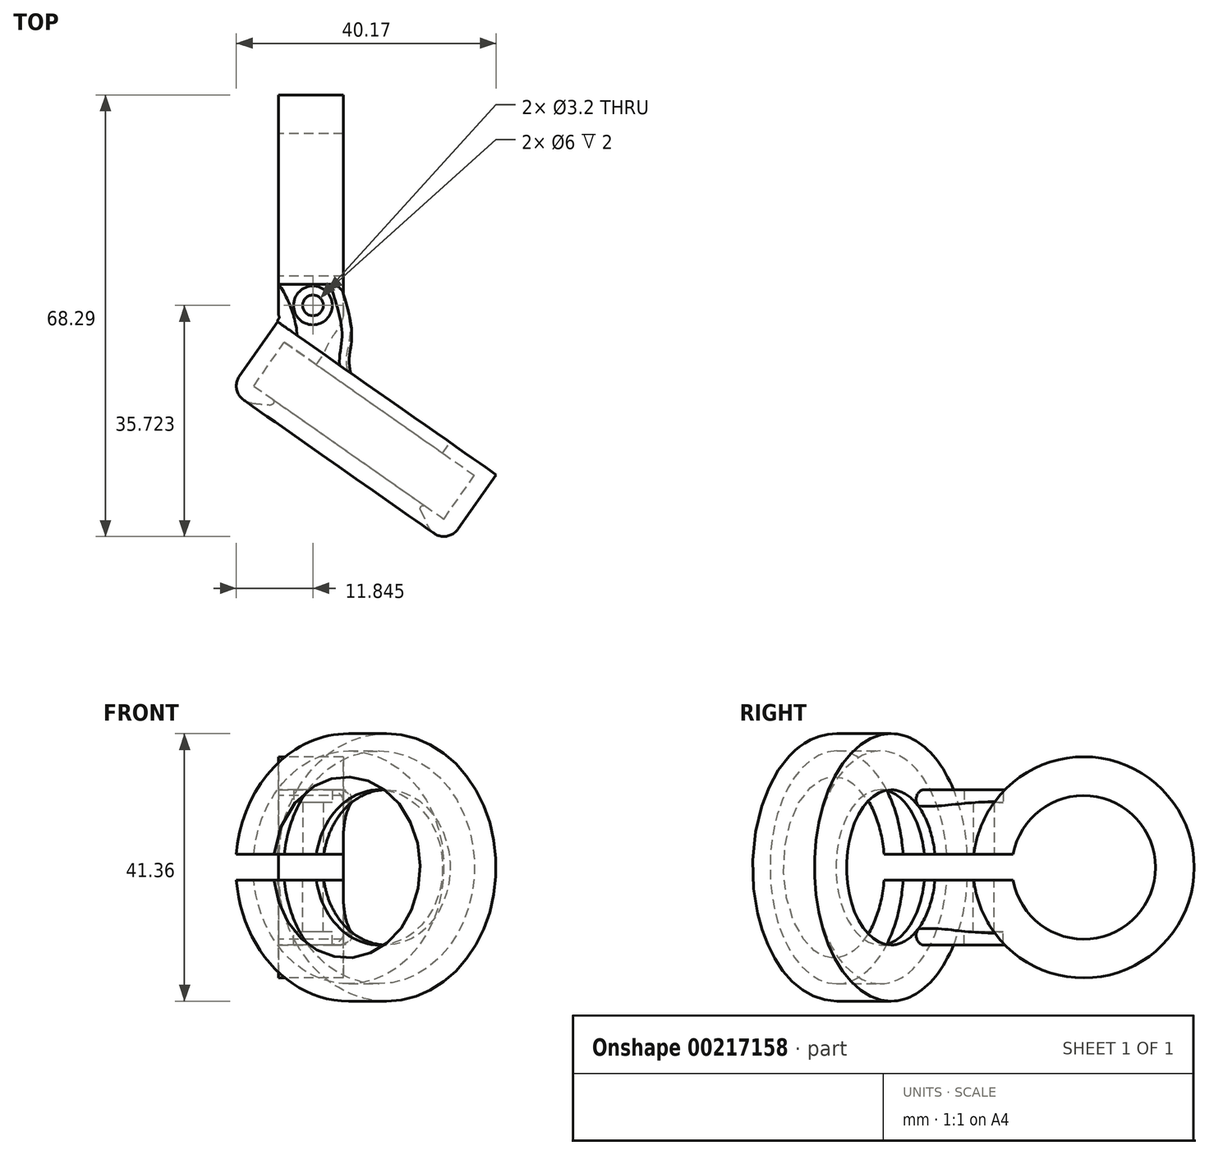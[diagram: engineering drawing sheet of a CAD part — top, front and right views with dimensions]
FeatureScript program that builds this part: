
annotation { "Feature Type Name" : "Feature", "Feature Type Description" : "" }
export const myFeature = defineFeature(function(context is Context, id is Id, definition is map)
    precondition{}
    {
        {
            var Q0;
            Q0=qCreatedBy(makeId("Top.planeOp"),FACE);
            var sketch = newSketch(context, id + "F0", { "sketchPlane" : qUnion([Q0])});
            skLineSegment(sketch, "E0.bottom", {"start": v(-17.11, 22.2) * mm, "end": v(17.11, 22.2) * mm});
            skLineSegment(sketch, "E0.top", {"start": v(-17.11, 0) * mm, "end": v(17.11, 0) * mm});
            skLineSegment(sketch, "E0.left", {"start": v(-17.11, 22.2) * mm, "end": v(-17.11, 0) * mm});
            skLineSegment(sketch, "E0.right", {"start": v(17.11, 22.2) * mm, "end": v(17.11, 0) * mm});
            skLineSegment(sketch, "E1", {"start": v(-12.38, -10) * mm, "end": v(-17.11, -16.76) * mm});
            skLineSegment(sketch, "E2", {"start": v(-17.11, -16.76) * mm, "end": v(12.38, -37.4) * mm});
            skLineSegment(sketch, "E3", {"start": v(12.38, -37.4) * mm, "end": v(17.11, -30.65) * mm});
            skLineSegment(sketch, "E4", {"start": v(17.11, -30.65) * mm, "end": v(-12.38, -10) * mm});
            skLineSegment(sketch, "E5", {"start": v(-2.37, -27.08) * mm, "end": v(2.37, -20.32) * mm});
            skLineSegment(sketch, "E6", {"start": v(-17.11, 11.1) * mm, "end": v(17.11, 11.1) * mm});
            skSolve(sketch);
        }
        {
            var Q0;
            Q0=qCreatedBy(makeId("Top.planeOp"),FACE);
            var sketch = newSketch(context, id + "F1", { "sketchPlane" : qUnion([Q0])});
            skLineSegment(sketch, "E7", {"start": v(-14.57, -19.67) * mm, "end": v(-17.34, -19.43) * mm});
            skArc(sketch, "E8", {"start": v(-14.57, -19.67) * mm, "mid": v(-14.06, -19.35) * mm, "end": v(-14.24, -18.77) * mm});
            skLineSegment(sketch, "E9", {"start": v(-14.24, -18.77) * mm, "end": v(-17.11, -16.76) * mm});
            skLineSegment(sketch, "E10", {"start": v(-17.11, -16.76) * mm, "end": v(-12.38, -10) * mm});
            skArc(sketch, "E11", {"start": v(-19.3, -15.22) * mm, "mid": v(-19.54, -17.9) * mm, "end": v(-17.34, -19.43) * mm});
            skLineSegment(sketch, "E12", {"start": v(-19.3, -15.22) * mm, "end": v(-13.43, -6.82) * mm});
            skLineSegment(sketch, "E13", {"start": v(-12.38, -10) * mm, "end": v(-7.46, -13.44) * mm});
            skLineSegment(sketch, "E14", {"start": v(-7.46, -13.44) * mm, "end": v(-6.32, -11.8) * mm});
            skLineSegment(sketch, "E15", {"start": v(-6.32, -11.8) * mm, "end": v(-13.43, -6.82) * mm});
            skSolve(sketch);
        }
        {
            var Q0;
            Q0 = qSketchRegion(id + "F1", true);
            var Q1;
            Q1=sQuery(id+"F0.wireOp",EDGE,"E5");
            revolve(context, id + "F2", {"entities" : qUnion([Q0]), "axis" : qUnion([Q1]), "revolveType" : RevolveType.ONE_DIRECTION, "oppositeDirection" : true, "angle" : 180 * degree});
        }
        {
            var Q0;
            Q0=qCreatedBy(makeId("Top.planeOp"),FACE);
            var sketch = newSketch(context, id + "F3", { "sketchPlane" : qUnion([Q0])});
            skLineSegment(sketch, "E16", {"start": v(-13.17, 0) * mm, "end": v(-13.17, -6) * mm});
            skLineSegment(sketch, "E17", {"start": v(-13.17, -6) * mm, "end": v(-3.17, -6) * mm});
            skLineSegment(sketch, "E18", {"start": v(-3.17, -6) * mm, "end": v(-3.17, 0) * mm});
            skLineSegment(sketch, "E19", {"start": v(-3.17, 0) * mm, "end": v(-13.17, 0) * mm});
            skArc(sketch, "E20", {"start": v(-13.43, -6.82) * mm, "mid": v(-13.24, -6.43) * mm, "end": v(-13.17, -6) * mm, "construction": true});
            skSolve(sketch);
        }
        {
            var Q0;
            Q0=makeQuery(id+"F3.imprint","IMPRINT",FACE,{"disambiguationData":[TD([[makeQuery(id+"F3.imprint","IMPRINT",EDGE,{"derivedFrom":sQuery(id+"F3.wireOp",EDGE,"E16")}),1.0]])]});
            var Q1;
            Q1=sQuery(id+"F0.wireOp",EDGE,"E6");
            revolve(context, id + "F4", {"entities" : qUnion([Q0]), "axis" : qUnion([Q1]), "revolveType" : RevolveType.ONE_DIRECTION, "angle" : 180 * degree});
        }
        {
            var Q0;
            Q0=qCreatedBy(makeId("Top.planeOp"),FACE);
            cPlane(context, id + "F5", {"entities" : qUnion([Q0]), "cplaneType" : CPlaneType.OFFSET, "offset" : 12 * mm, "oppositeDirection" : true, "width" : 150 * mm, "height" : 150 * mm});
        }
        {
            var Q0;
            Q0=qCreatedBy(id+"F5.planeOp",FACE);
            var sketch = newSketch(context, id + "F6", { "sketchPlane" : qUnion([Q0])});
            skLineSegment(sketch, "E21", {"start": v(-13.17, -1.08) * mm, "end": v(-3.17, -1.08) * mm});
            skLineSegment(sketch, "E22", {"start": v(-3.17, 23.28) * mm, "end": v(-13.17, 23.28) * mm});
            skLineSegment(sketch, "E23", {"start": v(3.51, -18.69) * mm, "end": v(-10.29, -9.02) * mm});
            skLineSegment(sketch, "E24", {"start": v(3.51, -18.69) * mm, "end": v(-3.17, -1.08) * mm});
            skArc(sketch, "E25", {"start": v(-10.29, -9.02) * mm, "mid": v(-11.21, -4.87) * mm, "end": v(-13.17, -1.08) * mm});
            skSolve(sketch);
        }
        {
            var Q0;
            Q0=makeQuery(id+"F4.opRevolve","CAP_FACE",FACE,{"disambiguationData":[OSD([sQuery(id+"F3.wireOp",EDGE,"E16"),sQuery(id+"F3.wireOp",EDGE,"E17"),sQuery(id+"F3.wireOp",EDGE,"E18"),sQuery(id+"F3.wireOp",EDGE,"E19")])],"isStart":true});
            var sketch = newSketch(context, id + "F7", { "sketchPlane" : qUnion([Q0])});
            skLineSegment(sketch, "E26", {"start": v(-13.17, -6) * mm, "end": v(-3.17, -6) * mm});
            skLineSegment(sketch, "E27", {"start": v(-3.17, -6) * mm, "end": v(-6.32, -11.8) * mm});
            skLineSegment(sketch, "E28", {"start": v(-6.32, -11.8) * mm, "end": v(-13.43, -6.82) * mm});
            skArc(sketch, "E29.0", {"start": v(-13.43, -6.82) * mm, "mid": v(-13.24, -6.43) * mm, "end": v(-13.17, -6) * mm});
            skSolve(sketch);
        }
        {
            var Q0;
            Q0=makeQuery(id+"F4.opRevolve","SWEPT_FACE",FACE,{"disambiguationData":[OSD([sQuery(id+"F3.wireOp",EDGE,"E16")])]});
            var sketch = newSketch(context, id + "F8", { "sketchPlane" : qUnion([Q0])});
            skArc(sketch, "E30.0", {"start": v(1.08, -12) * mm, "mid": v(4.72, -6.48) * mm, "end": v(6, 0) * mm});
            skPoint(sketch, "E31", {"position": v(1.08, -12) * mm});
            skPoint(sketch, "E32.orphan", {"position": v(-28.2, 0) * mm});
            skSolve(sketch);
        }
        {
            var Q0;
            Q0=makeQuery(id+"F2.opRevolve","SWEPT_FACE",FACE,{"disambiguationData":[OSD([sQuery(id+"F1.wireOp",EDGE,"E15")])]});
            var sketch = newSketch(context, id + "F9", { "sketchPlane" : qUnion([Q0])});
            skArc(sketch, "E33.0", {"start": v(-13.6, -12) * mm, "mid": v(-5.11, -8.49) * mm, "end": v(-1.6, 0) * mm});
            skArc(sketch, "E33.1", {"start": v(3.25, -12) * mm, "mid": v(6.1, -6.3) * mm, "end": v(7.09, 0) * mm});
            skPoint(sketch, "E34", {"position": v(-13.6, -12) * mm});
            skPoint(sketch, "E35", {"position": v(3.25, -12) * mm});
            skSolve(sketch);
        }
        {
            var Q0;
            Q0=makeQuery(id+"F4.opRevolve","SWEPT_FACE",FACE,{"disambiguationData":[OSD([sQuery(id+"F3.wireOp",EDGE,"E18")])]});
            var sketch = newSketch(context, id + "F10", { "sketchPlane" : qUnion([Q0])});
            skArc(sketch, "E36.0", {"start": v(-1.08, -12) * mm, "mid": v(-4.72, -6.48) * mm, "end": v(-6, 0) * mm});
            skPoint(sketch, "E37", {"position": v(-1.08, -12) * mm});
            skSolve(sketch);
        }
        {
            var Q2;
            Q2=makeQuery(id+"F7.imprint","IMPRINT",FACE,{"disambiguationData":[TD([[makeQuery(id+"F7.imprint","IMPRINT",EDGE,{"derivedFrom":sQuery(id+"F7.wireOp",EDGE,"E26")}),-1.0]])]});
            var Q3;
            Q3=makeQuery(id+"F6.imprint","IMPRINT",FACE,{"disambiguationData":[TD([[makeQuery(id+"F6.imprint","IMPRINT",EDGE,{"derivedFrom":sQuery(id+"F6.wireOp",EDGE,"E21")}),-1.0]])]});
            var Q4;
            Q4=sQuery(id+"F9.wireOp",EDGE,"E33.0");
            var Q5;
            Q5=sQuery(id+"F10.wireOp",EDGE,"E36.0");
            var Q6;
            Q6=sQuery(id+"F8.wireOp",EDGE,"E30.0");
            var Q7;
            Q7=sQuery(id+"F9.wireOp",EDGE,"E33.1");
            loft(context, id + "F11", {"operationType" : NewBodyOperationType.ADD, "addGuides" : true, "sheetProfilesArray" : [{ "sheetProfileEntities" : qUnion([Q2]) }, { "sheetProfileEntities" : qUnion([Q3]) }], "guidesArray" : [{ "guideEntities" : qUnion([Q4]), "guideDerivativeType" : LoftGuideDerivativeType.DEFAULT, "guideDerivativeMagnitude" : 1 }, { "guideEntities" : qUnion([Q5]), "guideDerivativeType" : LoftGuideDerivativeType.DEFAULT, "guideDerivativeMagnitude" : 1 }, { "guideEntities" : qUnion([Q6]), "guideDerivativeType" : LoftGuideDerivativeType.DEFAULT, "guideDerivativeMagnitude" : 1 }, { "guideEntities" : qUnion([Q7]), "guideDerivativeType" : LoftGuideDerivativeType.DEFAULT, "guideDerivativeMagnitude" : 1 }]});
        }
        {
            var Q0;
            Q0=qCreatedBy(makeId("Top.planeOp"),FACE);
            var sketch = newSketch(context, id + "F12", { "sketchPlane" : qUnion([Q0])});
            skLineSegment(sketch, "E38.bottom", {"start": v(-24.47, 6.44) * mm, "end": v(1.46, 6.44) * mm});
            skLineSegment(sketch, "E38.top", {"start": v(-24.47, -24.77) * mm, "end": v(1.46, -24.77) * mm});
            skLineSegment(sketch, "E38.left", {"start": v(-24.47, 6.44) * mm, "end": v(-24.47, -24.77) * mm});
            skLineSegment(sketch, "E38.right", {"start": v(1.46, 6.44) * mm, "end": v(1.46, -24.77) * mm});
            skSolve(sketch);
        }
        {
            var Q0;
            Q0=makeQuery(id+"F12.imprint","IMPRINT",FACE,{"disambiguationData":[TD([[makeQuery(id+"F12.imprint","IMPRINT",EDGE,{"derivedFrom":sQuery(id+"F12.wireOp",EDGE,"E38.bottom")}),-1.0]])]});
            extrude(context, id + "F13", {"entities" : qUnion([Q0]), "operationType" : NewBodyOperationType.REMOVE, "oppositeDirection" : true, "depth" : 2 * mm});
        }
        {
            var Q0;
            Q0=qCreatedBy(makeId("Top.planeOp"),FACE);
            var sketch = newSketch(context, id + "F14", { "sketchPlane" : qUnion([Q0])});
            skCircle(sketch, "E39", {"center": v(-7.86, -4.37) * mm, "radius": 1.6 * mm});
            skSolve(sketch);
        }
        {
            var Q0;
            Q0 = qSketchRegion(id + "F14", true);
            extrude(context, id + "F15", {"entities" : qUnion([Q0]), "operationType" : NewBodyOperationType.REMOVE, "oppositeDirection" : true, "depth" : 10 * mm});
        }
        {
            var Q0;
            Q0=makeQuery(id+"F15.boolean.opBoolean","COPY",FACE,{"derivedFrom":makeQuery(id+"F15.opExtrude","CAP_FACE",FACE,{"disambiguationData":[OSD([sQuery(id+"F14.wireOp",EDGE,"E39")])],"isStart":false})});
            var sketch = newSketch(context, id + "F16", { "sketchPlane" : qUnion([Q0])});
            skCircle(sketch, "E40", {"center": v(-7.86, -4.37) * mm, "radius": 3 * mm});
            skSolve(sketch);
        }
        {
            var Q0;
            Q0 = qSketchRegion(id + "F16", true);
            extrude(context, id + "F17", {"entities" : qUnion([Q0]), "operationType" : NewBodyOperationType.REMOVE, "oppositeDirection" : true, "depth" : 25 * mm});
        }
        {
            var Q0;
            Q0=makeQuery(id+"F11.opLoft","MID_CAP_EDGE",EDGE,{"disambiguationData":[OSD([sQuery(id+"F6.wireOp",EDGE,"E24"),sQuery(id+"F9.wireOp",EDGE,"E33.0"),sQuery(id+"F10.wireOp",EDGE,"E36.0")])],"capPos":1.0});
            fillet(context, id + "F18", {"entities" : qUnion([Q0]), "radius" : 1.5 * mm, "tangentPropagation" : true, "allowEdgeOverflow" : false});
        }
        {
            var Q0;
            Q0=makeQuery(id+"F2.opRevolve","SWEPT_BODY",BODY,{"disambiguationData":[OSD([sQuery(id+"F1.wireOp",EDGE,"E7"),sQuery(id+"F1.wireOp",EDGE,"E8"),sQuery(id+"F1.wireOp",EDGE,"E9"),sQuery(id+"F1.wireOp",EDGE,"E10"),sQuery(id+"F1.wireOp",EDGE,"E11"),sQuery(id+"F1.wireOp",EDGE,"E12"),sQuery(id+"F1.wireOp",EDGE,"E13"),sQuery(id+"F1.wireOp",EDGE,"E14"),sQuery(id+"F1.wireOp",EDGE,"E15")])]});
            var Q1;
            Q1=makeQuery(id+"F2.opRevolve","CAP_FACE",FACE,{"disambiguationData":[OSD([sQuery(id+"F1.wireOp",EDGE,"E7"),sQuery(id+"F1.wireOp",EDGE,"E8"),sQuery(id+"F1.wireOp",EDGE,"E9"),sQuery(id+"F1.wireOp",EDGE,"E10"),sQuery(id+"F1.wireOp",EDGE,"E11"),sQuery(id+"F1.wireOp",EDGE,"E12"),sQuery(id+"F1.wireOp",EDGE,"E13"),sQuery(id+"F1.wireOp",EDGE,"E14"),sQuery(id+"F1.wireOp",EDGE,"E15")])],"isStart":false});
            mirror(context, id + "F19", {"operationType" : NewBodyOperationType.ADD, "entities" : qUnion([Q0]), "mirrorPlane" : qUnion([Q1])});
        }
    });
